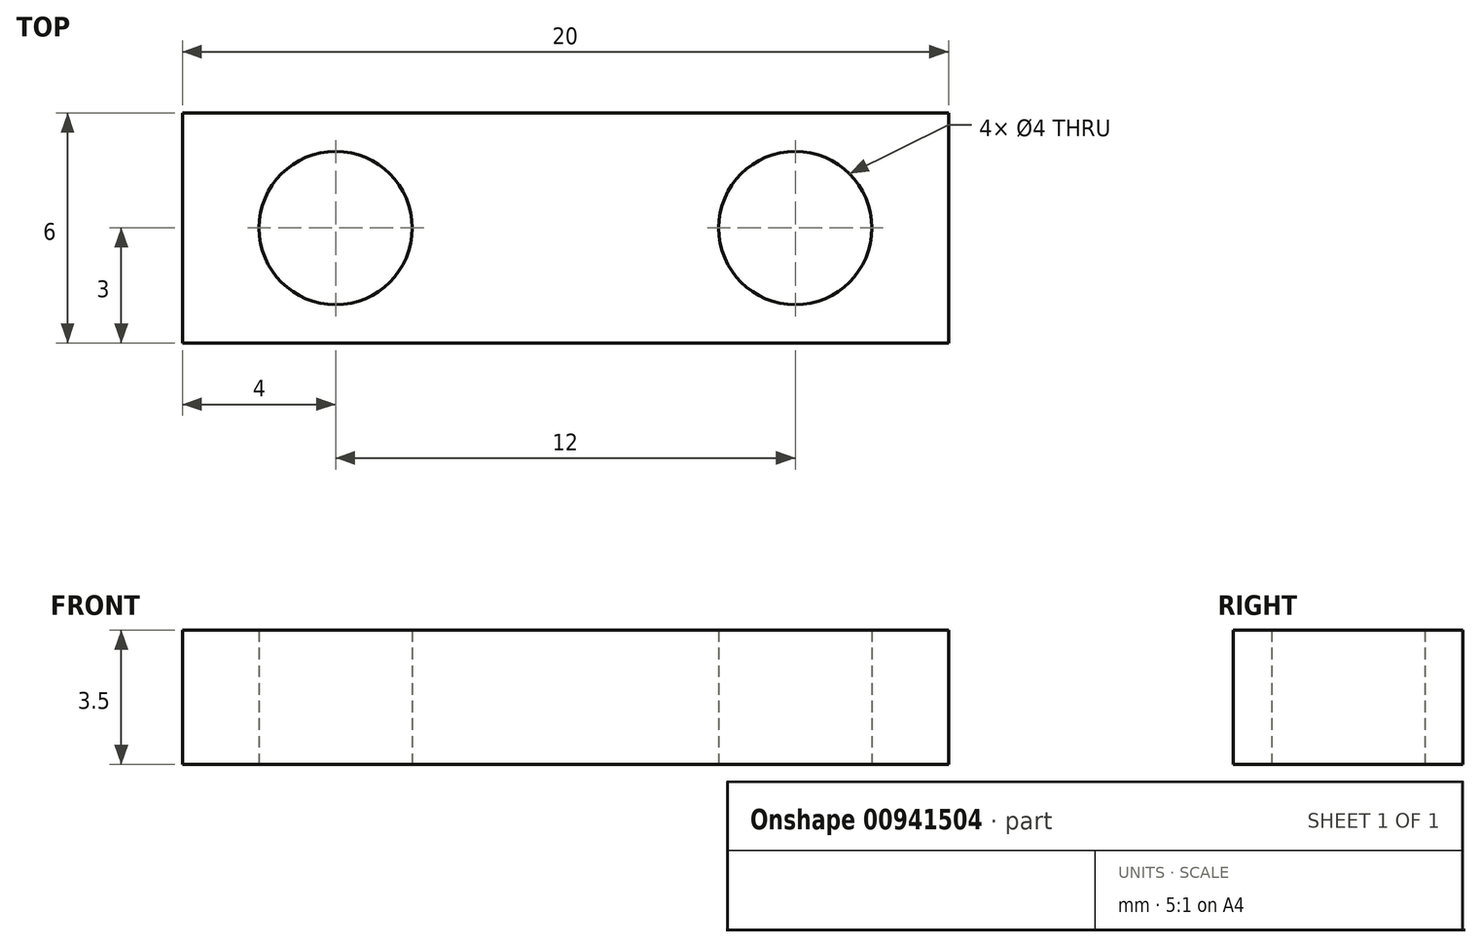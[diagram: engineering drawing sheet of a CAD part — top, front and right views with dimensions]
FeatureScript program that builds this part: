
annotation { "Feature Type Name" : "Feature", "Feature Type Description" : "" }
export const myFeature = defineFeature(function(context is Context, id is Id, definition is map)
    precondition{}
    {
        {
            var Q0;
            Q0=qCreatedBy(makeId("Top.planeOp"),FACE);
            var sketch = newSketch(context, id + "F0", { "sketchPlane" : qUnion([Q0])});
            skLineSegment(sketch, "E0.bottom", {"start": v(10, 3) * mm, "end": v(-10, 3) * mm});
            skLineSegment(sketch, "E0.top", {"start": v(10, -3) * mm, "end": v(-10, -3) * mm});
            skLineSegment(sketch, "E0.left", {"start": v(10, 3) * mm, "end": v(10, -3) * mm});
            skLineSegment(sketch, "E0.right", {"start": v(-10, 3) * mm, "end": v(-10, -3) * mm});
            skPoint(sketch, "E0.middle", {"position": v(0, 0) * mm});
            skLineSegment(sketch, "E1", {"start": v(0, 4.94) * mm, "end": v(0, -4.5) * mm, "construction": true});
            skPoint(sketch, "E1.endSnap0", {"position": v(0, -3) * mm});
            skCircle(sketch, "E2", {"center": v(-6, 0) * mm, "radius": 2 * mm});
            skPoint(sketch, "E2.centerSnap0", {"position": v(-10, 0) * mm});
            skCircle(sketch, "E3", {"center": v(6, 0) * mm, "radius": 2 * mm});
            skPoint(sketch, "E3.centerSnap0", {"position": v(10, 0) * mm});
            skSolve(sketch);
        }
        {
            var Q0;
            Q0=makeQuery(id+"F0.imprint","IMPRINT",FACE,{"disambiguationData":[TD([[makeQuery(id+"F0.imprint","IMPRINT",EDGE,{"derivedFrom":sQuery(id+"F0.wireOp",EDGE,"E0.bottom")}),1.0]])]});
            extrude(context, id + "F1", {"entities" : qUnion([Q0]), "depth" : 3.5 * mm, "offsetDistance" : 25 * mm});
        }
    });
